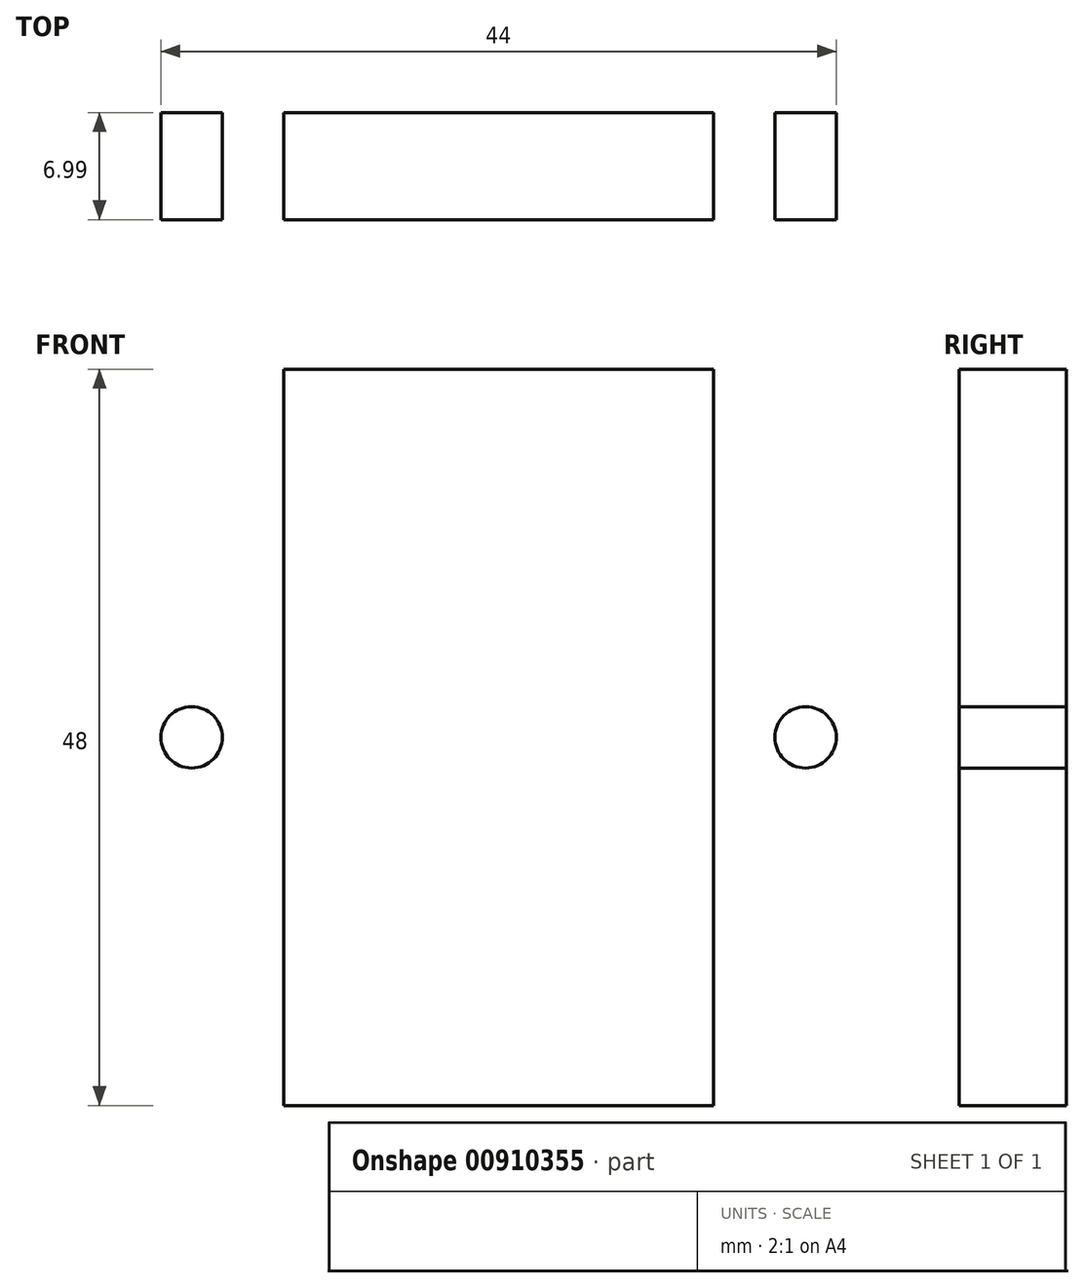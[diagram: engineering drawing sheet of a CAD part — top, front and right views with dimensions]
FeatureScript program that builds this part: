
annotation { "Feature Type Name" : "Feature", "Feature Type Description" : "" }
export const myFeature = defineFeature(function(context is Context, id is Id, definition is map)
    precondition{}
    {
        {
            var Q0;
            Q0=qCreatedBy(makeId("Front.planeOp"),FACE);
            var sketch = newSketch(context, id + "F0", { "sketchPlane" : qUnion([Q0])});
            skLineSegment(sketch, "E0.bottom", {"start": v(14, 24) * mm, "end": v(-14, 24) * mm});
            skLineSegment(sketch, "E0.top", {"start": v(14, -24) * mm, "end": v(-14, -24) * mm});
            skLineSegment(sketch, "E0.left", {"start": v(14, 24) * mm, "end": v(14, -24) * mm});
            skLineSegment(sketch, "E0.right", {"start": v(-14, 24) * mm, "end": v(-14, -24) * mm});
            skPoint(sketch, "E0.middle", {"position": v(0, 0) * mm});
            skCircle(sketch, "E1", {"center": v(20, 0) * mm, "radius": 2 * mm});
            skCircle(sketch, "E2", {"center": v(-20, 0) * mm, "radius": 2 * mm});
            skLineSegment(sketch, "E3", {"start": v(20, 0) * mm, "end": v(-20, 0) * mm, "construction": true});
            skSolve(sketch);
        }
        {
            var Q0;
            Q0 = qSketchRegion(id + "F0", true);
            extrude(context, id + "F1", {"entities" : qUnion([Q0]), "depth" : 7 * mm, "offsetDistance" : 25.4 * mm});
        }
    });
